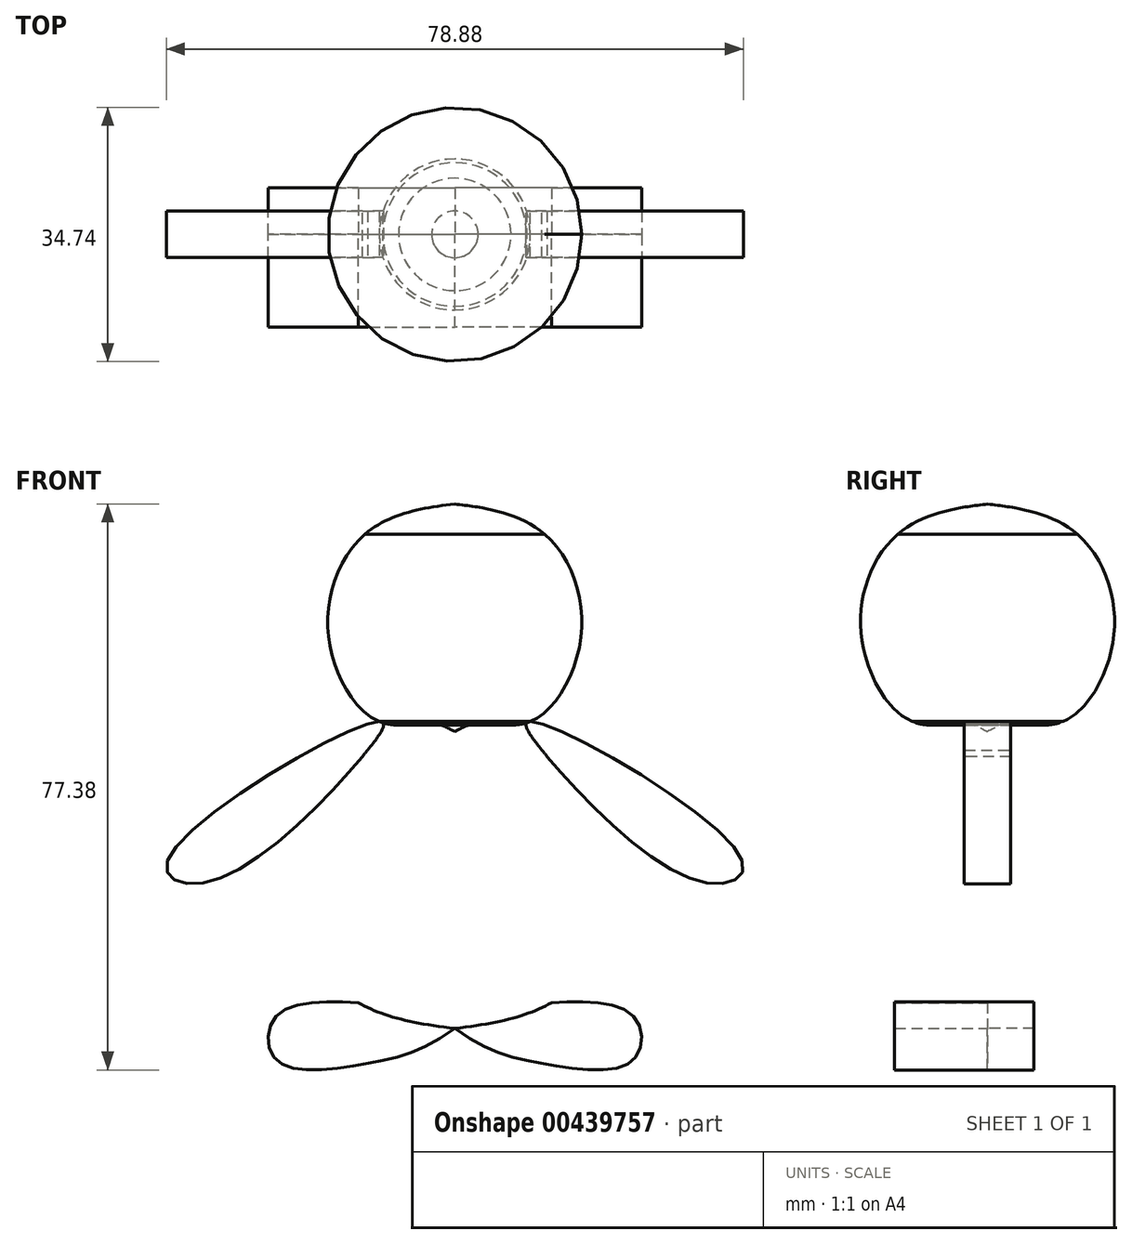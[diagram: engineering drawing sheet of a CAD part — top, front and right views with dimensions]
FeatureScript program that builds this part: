
annotation { "Feature Type Name" : "Feature", "Feature Type Description" : "" }
export const myFeature = defineFeature(function(context is Context, id is Id, definition is map)
    precondition{}
    {
        {
            var Q0;
            Q0=qCreatedBy(makeId("Front.planeOp"),FACE);
            var sketch = newSketch(context, id + "F0", { "sketchPlane" : qUnion([Q0])});
            skLineSegment(sketch, "E0", {"start": v(0, 76.3) * mm, "end": v(0, 0) * mm});
            skLineSegment(sketch, "E1", {"start": v(0, 76.3) * mm, "end": v(0, -75.3) * mm, "construction": true});
            skLineSegment(sketch, "E2", {"start": v(0, -31.17) * mm, "end": v(0, 9.46) * mm});
            skFitSpline(sketch, "E3", {"points": [v(0, 9.46) * mm, v(8.2, 10.06) * mm, v(20.06, -10.23) * mm, v(16.77, -24.77) * mm, v(0, -31.17) * mm], "startDerivative": vector(45.57, 17.4) * mm, "endDerivative": vector(-94.82, -11) * mm});
            skFitSpline(sketch, "E4", {"points": [v(12.62, 6.02) * mm, v(34.22, -11.24) * mm, v(39.27, -8.2) * mm, v(10.33, 10.81) * mm, v(12.62, 6.02) * mm]});
            skFitSpline(sketch, "E5.MirrorC", {"points": [v(-12.62, 6.02) * mm, v(-34.22, -11.24) * mm, v(-39.27, -8.2) * mm, v(-10.33, 10.81) * mm, v(-12.62, 6.02) * mm]});
            skFitSpline(sketch, "E6.MirrorCS", {"points": [v(0, 9.46) * mm, v(-8.2, 10.06) * mm, v(-20.06, -10.23) * mm, v(-16.77, -24.77) * mm, v(0, -31.17) * mm], "startDerivative": vector(-45.57, 17.4) * mm, "endDerivative": vector(94.82, -11) * mm});
            skFitSpline(sketch, "E7", {"points": [v(13.22, -27.64) * mm, v(24.4, -29.46) * mm, v(24.4, -35.47) * mm, v(13.22, -36.18) * mm, v(0, -31.17) * mm], "startDerivative": vector(47.14, 2.64) * mm, "endDerivative": vector(-48.5, 35.21) * mm});
            skFitSpline(sketch, "E8.MirrorCS", {"points": [v(-13.22, -27.64) * mm, v(-24.4, -29.46) * mm, v(-24.4, -35.47) * mm, v(-13.22, -36.18) * mm, v(0, -31.17) * mm], "startDerivative": vector(-47.14, 2.64) * mm, "endDerivative": vector(48.5, 35.21) * mm});
            skLineSegment(sketch, "E9", {"start": v(0, 71.92) * mm, "end": v(0, 38.15) * mm});
            skFitSpline(sketch, "E10", {"points": [v(0, 71.92) * mm, v(-28.13, 66.2) * mm, v(-36.89, 53.73) * mm, v(-29.48, 34.87) * mm, v(-12.29, 36.4) * mm, v(0, 38.15) * mm], "startDerivative": vector(-127.08, -12.71) * mm, "endDerivative": vector(69.2, 4.8) * mm});
            skLineSegment(sketch, "E11", {"start": v(0, 40.54) * mm, "end": v(0, 9.46) * mm});
            skFitSpline(sketch, "E12", {"points": [v(0, 40.54) * mm, v(-12.29, 36.4) * mm, v(-17.3, 22.86) * mm, v(-10.33, 10.81) * mm, v(-2.75, 10.5) * mm, v(0, 9.46) * mm], "startDerivative": vector(-58.86, -6.73) * mm, "endDerivative": vector(18.95, -7.3) * mm});
            skFitSpline(sketch, "E13.MirrorCS", {"points": [v(0, 40.54) * mm, v(12.29, 36.4) * mm, v(17.3, 22.86) * mm, v(10.33, 10.81) * mm, v(2.75, 10.5) * mm, v(0, 9.46) * mm], "startDerivative": vector(58.86, -6.73) * mm, "endDerivative": vector(-18.95, -7.3) * mm});
            skFitSpline(sketch, "E14.MirrorCS", {"points": [v(0, 71.92) * mm, v(28.13, 66.2) * mm, v(36.89, 53.73) * mm, v(29.48, 34.87) * mm, v(12.29, 36.4) * mm, v(0, 38.15) * mm], "startDerivative": vector(127.08, -12.71) * mm, "endDerivative": vector(-69.2, 4.8) * mm});
            skSolve(sketch);
        }
        {
            var Q0;
            {var subQ0=sQuery(id+"F0.wireOp",EDGE,"E9");Q0=makeQuery(id+"F0.imprint","IMPRINT",FACE,{"disambiguationData":[TD([[makeQuery(id+"F0.imprint","IMPRINT",EDGE,{"derivedFrom":subQ0}),-1.0]])]});}
            var Q1;
            {var subQ3=sQuery(id+"F0.wireOp",EDGE,"E12");var subQ9=sQuery(id+"F0.wireOp",EDGE,"E5.MirrorC");var subQ10=makeQuery(id+"F0.imprint","INTERSECT",VERTEX,{"disambiguationData":[OD(0.0)],"derivedFrom":[subQ9,subQ3]});Q1=makeQuery(id+"F0.imprint","IMPRINT",FACE,{"disambiguationData":[TD([[makeQuery(id+"F0.imprint","IMPRINT",EDGE,{"disambiguationData":[TD([[subQ10,-1.0]])],"derivedFrom":subQ9}),1.0]])]});}
            var Q2;
            {var subQ0=sQuery(id+"F0.wireOp",EDGE,"E13.MirrorCS");var subQ1=sQuery(id+"F0.wireOp",EDGE,"E3");var subQ5=makeQuery(id+"F0.imprint","INTERSECT",VERTEX,{"disambiguationData":[OD(0.0)],"derivedFrom":[subQ1,subQ0]});Q2=makeQuery(id+"F0.imprint","IMPRINT",FACE,{"disambiguationData":[TD([[makeQuery(id+"F0.imprint","IMPRINT",EDGE,{"disambiguationData":[TD([[subQ5,-1.0]])],"derivedFrom":subQ1}),-1.0]])]});}
            var Q3;
            {var subQ1=sQuery(id+"F0.wireOp",EDGE,"E10");var subQ3=sQuery(id+"F0.wireOp",EDGE,"E12");var subQ4=makeQuery(id+"F0.imprint","INTERSECT",VERTEX,{"derivedFrom":[subQ1,subQ3]});Q3=makeQuery(id+"F0.imprint","IMPRINT",FACE,{"disambiguationData":[TD([[makeQuery(id+"F0.imprint","IMPRINT",EDGE,{"disambiguationData":[TD([[subQ4,-1.0]])],"derivedFrom":subQ1}),1.0]])]});}
            var Q4;
            Q4=sQuery(id+"F0.wireOp",EDGE,"E1");
            revolve(context, id + "F1", {"entities" : qUnion([Q0, Q1, Q2, Q3]), "axis" : qUnion([Q4]), "revolveType" : RevolveType.FULL});
        }
        {
            var Q0;
            {var subQ0=sQuery(id+"F0.wireOp",EDGE,"E4");var subQ1=sQuery(id+"F0.wireOp",EDGE,"E3");var subQ2=makeQuery(id+"F0.imprint","INTERSECT",VERTEX,{"disambiguationData":[OD(0.0)],"derivedFrom":[subQ1,subQ0]});Q0=makeQuery(id+"F0.imprint","IMPRINT",FACE,{"disambiguationData":[TD([[makeQuery(id+"F0.imprint","IMPRINT",EDGE,{"disambiguationData":[TD([[subQ2,1.0]])],"derivedFrom":subQ1}),1.0]])]});}
            var Q1;
            {var subQ0=sQuery(id+"F0.wireOp",EDGE,"E12");var subQ1=sQuery(id+"F0.wireOp",EDGE,"E5.MirrorC");var subQ2=makeQuery(id+"F0.imprint","INTERSECT",VERTEX,{"disambiguationData":[OD(0.0)],"derivedFrom":[subQ1,subQ0]});Q1=makeQuery(id+"F0.imprint","IMPRINT",FACE,{"disambiguationData":[TD([[makeQuery(id+"F0.imprint","IMPRINT",EDGE,{"disambiguationData":[TD([[subQ2,1.0]])],"derivedFrom":subQ1}),-1.0]])]});}
            extrude(context, id + "F2", {"entities" : qUnion([Q0, Q1]), "endBound" : BoundingType.SYMMETRIC, "depth" : 6.35 * mm});
        }
        {
            var Q0;
            {var subQ0=sQuery(id+"F0.wireOp",EDGE,"E7");Q0=makeQuery(id+"F0.imprint","IMPRINT",FACE,{"disambiguationData":[TD([[makeQuery(id+"F0.imprint","IMPRINT",EDGE,{"derivedFrom":subQ0}),-1.0]])]});}
            var Q1;
            {var subQ0=sQuery(id+"F0.wireOp",EDGE,"E8.MirrorCS");Q1=makeQuery(id+"F0.imprint","IMPRINT",FACE,{"disambiguationData":[TD([[makeQuery(id+"F0.imprint","IMPRINT",EDGE,{"derivedFrom":subQ0}),1.0]])]});}
            extrude(context, id + "F3", {"entities" : qUnion([Q0, Q1]), "depth" : 12.7 * mm});
        }
        {
            var Q0;
            {var subQ0=sQuery(id+"F0.wireOp",EDGE,"E7");Q0=makeQuery(id+"F0.imprint","IMPRINT",FACE,{"disambiguationData":[TD([[makeQuery(id+"F0.imprint","IMPRINT",EDGE,{"derivedFrom":subQ0}),-1.0]])]});}
            var Q1;
            {var subQ0=sQuery(id+"F0.wireOp",EDGE,"E8.MirrorCS");Q1=makeQuery(id+"F0.imprint","IMPRINT",FACE,{"disambiguationData":[TD([[makeQuery(id+"F0.imprint","IMPRINT",EDGE,{"derivedFrom":subQ0}),1.0]])]});}
            extrude(context, id + "F4", {"entities" : qUnion([Q0, Q1]), "oppositeDirection" : true, "depth" : 6.35 * mm});
        }
    });
